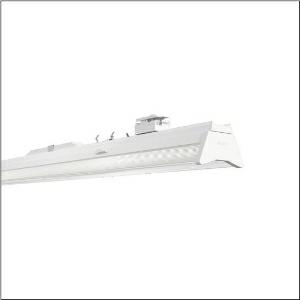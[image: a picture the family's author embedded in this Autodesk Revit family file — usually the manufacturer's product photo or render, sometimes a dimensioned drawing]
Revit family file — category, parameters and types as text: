
# Revit family: licross_r__21_performance_ho_52tm16dn4e5m_a06b
name_source: partatom
category: Lighting Fixtures
units: mm (PartAtom-declared; Revit-internal decimal feet)

## family parameters
Cut with Voids When Loaded = No
Host = Face
Light Source = No
Part Type = Normal
Room Calculation Point = No
Round Connector Dimension = Use Diameter
Shared = No

## types (1)
- --- (1 x LED, 14870 lm, 84.9 W, 4000K)
    Apparent Load = 85 VA
    CIE Flux Codes = 63 87 95 78 100
    Color Rendering = 80
    Color Temperature = 4000K
    Default Elevation = 1800 mm
    Description = Licross® 21 Performance HO, luminaire insert, of sheet steel, galvanised, coil coated, white, length: 1.500mm, width: 120mm, height: 123mm, LED rated luminous flux: 14.870lm, light colour: 840, control gear: DALI 2, with plug, 5-pole, with phase selection, mains connection: 220..240V, AC, 50/60Hz, rated input power: 85W, halogen-free wiring, primary light control with lens, of plastic, primary optical cover: cover, of PMMA, light emission: direct/indirect distribution, primary light characteristic: symmetric, protection rating (complete): IP40, insulation class (complete): insulation class I (protective earthing), certification: CE, ENEC, UKCA, protection symbol: D if used in an environment without relevant dust loads with corresponding accessories, impact resistance: IK06, permissible ambient temperature for indoor applications: -25..+35°C, corresponds to IFS (International Featured Standards) requirements for safety and quality in the food industry, reducing of maximum allowable ambient temperature of 5°C with ceiling mounting, LABS conformity tested according to VDMA 24364:2018-05, packaging unit: 1 piece
    Height = 114 mm
    Lamp = 1 x LED
    Lamp Light Flux = 14870 lm
    Lamp Power = 84.9 W
    Lamp count = 1
    Length = 1500 mm
    Luminous efficacy = 175 lm/W
    Manufacturer = Siteco
    ModVariant = No
    Model = 52TM16DN4E5M
    Mounting Place = Ceiling
    Mounting Type = Pendant
    Number of Poles = 1
    OnlyDefault = Yes
    Power Factor = 1
    Product Name = Licross® 21 Performance HO
    Product group = luminaire insert
    ProductGroupID = 902
    Protection Class = Protection class I
    Protection Degree = IP 40
    RLX_Detail_Level = 1
    RLX_Emergency_Light_Flux = 0 lm
    RLX_Emergency_Type = 0
    RLX_Emergency_Type_DB = No
    RlxData = <blob elided: 34037 chars, md5=68d8e92f>
    Socket = socket
    Standby Power = 0 W
    System Light Flux = 14870 lm
    System Power = 85 W
    Type Comments = factory setting: luminous flux: 100 % | dim-lin: 254 | 484 mA
    Type Image = l_1256138.jpg
    URL = http://relux.com
    VarID = @adj_129348
    Voltage = 0 V
    Weight = 0.00 kg
    Width = 120 mm

## geometry (parser evidence)
native form markers: Blend x4, Sweep x11
no freeform markers — native parametric forms only
